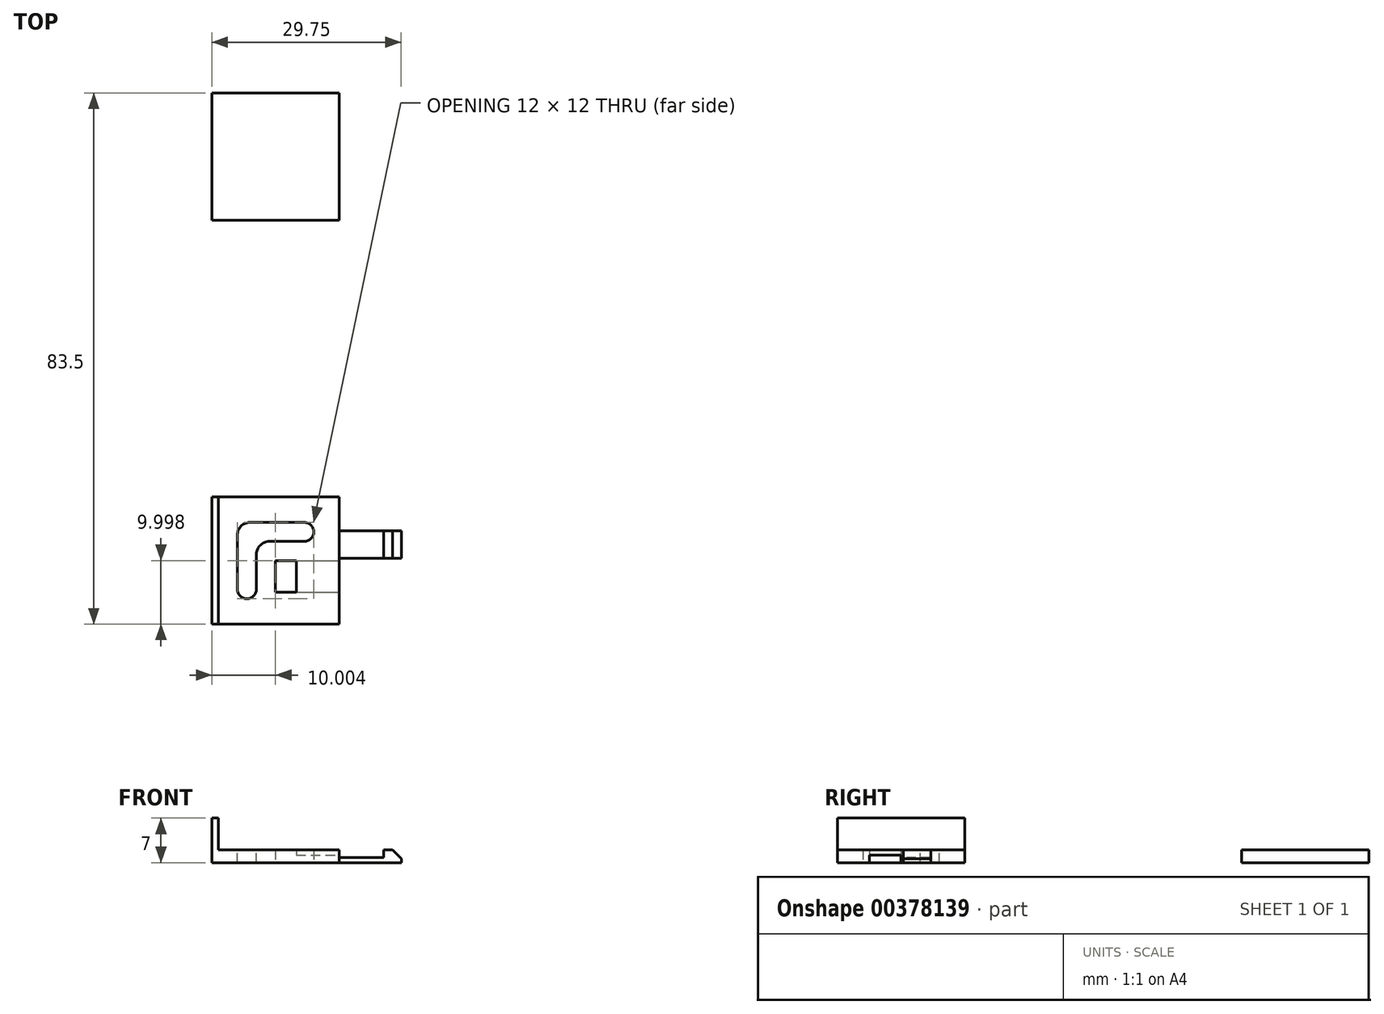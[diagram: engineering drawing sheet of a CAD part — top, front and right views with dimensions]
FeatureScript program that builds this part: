
annotation { "Feature Type Name" : "Feature", "Feature Type Description" : "" }
export const myFeature = defineFeature(function(context is Context, id is Id, definition is map)
    precondition{}
    {
        {
            var Q0;
            Q0=qCreatedBy(makeId("Top.planeOp"),FACE);
            var sketch = newSketch(context, id + "F0", { "sketchPlane" : qUnion([Q0])});
            skLineSegment(sketch, "E0.bottom", {"start": v(0.84, 22.12) * mm, "end": v(20.84, 22.12) * mm});
            skLineSegment(sketch, "E0.top", {"start": v(0.84, 42.12) * mm, "end": v(20.84, 42.12) * mm});
            skLineSegment(sketch, "E0.left", {"start": v(0.84, 22.12) * mm, "end": v(0.84, 42.12) * mm});
            skLineSegment(sketch, "E0.right", {"start": v(20.84, 22.12) * mm, "end": v(20.84, 42.12) * mm});
            skLineSegment(sketch, "E1.bottom", {"start": v(20.84, -21.38) * mm, "end": v(0.84, -21.38) * mm});
            skLineSegment(sketch, "E1.top", {"start": v(20.84, -41.38) * mm, "end": v(0.84, -41.38) * mm});
            skLineSegment(sketch, "E1.left", {"start": v(20.84, -21.38) * mm, "end": v(20.84, -41.38) * mm});
            skLineSegment(sketch, "E1.right", {"start": v(0.84, -21.38) * mm, "end": v(0.84, -41.38) * mm});
            skSolve(sketch);
        }
        {
            var Q0;
            Q0=makeQuery(id+"F0.imprint","IMPRINT",FACE,{"disambiguationData":[TD([[makeQuery(id+"F0.imprint","IMPRINT",EDGE,{"derivedFrom":sQuery(id+"F0.wireOp",EDGE,"E1.bottom")}),1.0]])]});
            var Q1;
            Q1=makeQuery(id+"F0.imprint","IMPRINT",FACE,{"disambiguationData":[TD([[makeQuery(id+"F0.imprint","IMPRINT",EDGE,{"derivedFrom":sQuery(id+"F0.wireOp",EDGE,"E0.bottom")}),1.0]])]});
            var Q2;
            Q2 = qSketchRegion(id + "F0", true);
            extrude(context, id + "F1", {"entities" : qUnion([Q0, Q1, Q2]), "depth" : 2 * mm});
        }
        {
            var Q0;
            Q0=makeQuery(id+"F1.opExtrude","SWEPT_FACE",FACE,{"disambiguationData":[OSD([sQuery(id+"F0.wireOp",EDGE,"E1.left")])]});
            var sketch = newSketch(context, id + "F2", { "sketchPlane" : qUnion([Q0])});
            skLineSegment(sketch, "E2.bottom", {"start": v(-36.38, 1.2) * mm, "end": v(-31.38, 1.2) * mm});
            skLineSegment(sketch, "E2.top", {"start": v(-36.38, 0) * mm, "end": v(-31.38, 0) * mm});
            skLineSegment(sketch, "E2.left", {"start": v(-36.38, 1.2) * mm, "end": v(-36.38, 0) * mm});
            skLineSegment(sketch, "E2.right", {"start": v(-31.38, 1.2) * mm, "end": v(-31.38, 0) * mm});
            skSolve(sketch);
        }
        {
            var Q0;
            Q0=makeQuery(id+"F2.imprint","IMPRINT",FACE,{"disambiguationData":[TD([[makeQuery(id+"F2.imprint","IMPRINT",EDGE,{"derivedFrom":sQuery(id+"F2.wireOp",EDGE,"E2.bottom")}),-1.0]])]});
            extrude(context, id + "F3", {"entities" : qUnion([Q0]), "operationType" : NewBodyOperationType.REMOVE, "oppositeDirection" : true, "depth" : 10 * mm});
        }
        {
            var Q0;
            Q0=makeQuery(id+"F3.boolean.opBoolean","COPY",FACE,{"derivedFrom":makeQuery(id+"F3.opExtrude","SWEPT_FACE",FACE,{"disambiguationData":[OSD([sQuery(id+"F2.wireOp",EDGE,"E2.bottom")])]})});
            var sketch = newSketch(context, id + "F4", { "sketchPlane" : qUnion([Q0])});
            skLineSegment(sketch, "E3.bottom", {"start": v(10.84, 36.38) * mm, "end": v(14.1, 36.38) * mm});
            skLineSegment(sketch, "E3.top", {"start": v(10.84, 31.38) * mm, "end": v(14.1, 31.38) * mm});
            skLineSegment(sketch, "E3.left", {"start": v(10.84, 36.38) * mm, "end": v(10.84, 31.38) * mm});
            skLineSegment(sketch, "E3.right", {"start": v(14.1, 36.38) * mm, "end": v(14.1, 31.38) * mm});
            skSolve(sketch);
        }
        {
            var Q0;
            Q0=makeQuery(id+"F4.imprint","IMPRINT",FACE,{"disambiguationData":[TD([[makeQuery(id+"F4.imprint","IMPRINT",EDGE,{"derivedFrom":sQuery(id+"F4.wireOp",EDGE,"E3.bottom")}),-1.0]])]});
            extrude(context, id + "F5", {"entities" : qUnion([Q0]), "operationType" : NewBodyOperationType.REMOVE, "endBound" : BoundingType.THROUGH_ALL, "oppositeDirection" : true, "depth" : 25 * mm});
        }
        {
            var Q0;
            Q0=makeQuery(id+"F1.opExtrude","SWEPT_FACE",FACE,{"disambiguationData":[OSD([sQuery(id+"F0.wireOp",EDGE,"E1.left")])]});
            var sketch = newSketch(context, id + "F6", { "sketchPlane" : qUnion([Q0])});
            skLineSegment(sketch, "E4.bottom", {"start": v(-26.73, 0.8) * mm, "end": v(-31.03, 0.8) * mm});
            skLineSegment(sketch, "E4.top", {"start": v(-26.73, 0) * mm, "end": v(-31.03, 0) * mm});
            skLineSegment(sketch, "E4.left", {"start": v(-26.73, 0.8) * mm, "end": v(-26.73, 0) * mm});
            skLineSegment(sketch, "E4.right", {"start": v(-31.03, 0.8) * mm, "end": v(-31.03, 0) * mm});
            skSolve(sketch);
        }
        {
            var Q0;
            Q0=makeQuery(id+"F6.imprint","IMPRINT",FACE,{"disambiguationData":[TD([[makeQuery(id+"F6.imprint","IMPRINT",EDGE,{"derivedFrom":sQuery(id+"F6.wireOp",EDGE,"E4.bottom")}),1.0]])]});
            extrude(context, id + "F7", {"entities" : qUnion([Q0]), "operationType" : NewBodyOperationType.ADD, "depth" : 9.75 * mm});
        }
        {
            var Q0;
            Q0=makeQuery(id+"F7.opExtrude","SWEPT_FACE",FACE,{"disambiguationData":[OSD([sQuery(id+"F6.wireOp",EDGE,"E4.bottom")])]});
            var sketch = newSketch(context, id + "F8", { "sketchPlane" : qUnion([Q0])});
            skLineSegment(sketch, "E5.bottom", {"start": v(30.6, -26.73) * mm, "end": v(27.84, -26.73) * mm});
            skLineSegment(sketch, "E5.top", {"start": v(30.6, -31.03) * mm, "end": v(27.84, -31.03) * mm});
            skLineSegment(sketch, "E5.left", {"start": v(30.6, -26.73) * mm, "end": v(30.6, -31.03) * mm});
            skLineSegment(sketch, "E5.right", {"start": v(27.84, -26.73) * mm, "end": v(27.84, -31.03) * mm});
            skSolve(sketch);
        }
        {
            var Q0;
            Q0=makeQuery(id+"F8.imprint","IMPRINT",FACE,{"disambiguationData":[TD([[makeQuery(id+"F8.imprint","IMPRINT",EDGE,{"derivedFrom":sQuery(id+"F8.wireOp",EDGE,"E5.bottom")}),1.0]])]});
            extrude(context, id + "F9", {"entities" : qUnion([Q0]), "operationType" : NewBodyOperationType.ADD, "depth" : 1.2 * mm});
        }
        {
            var Q0;
            Q0=makeQuery(id+"F9.opExtrude","CAP_EDGE",EDGE,{"disambiguationData":[OSD([sQuery(id+"F8.wireOp",EDGE,"E5.left")])],"isStart":false});
            chamfer(context, id + "F10", {"entities" : qUnion([Q0]), "width" : 1.4 * mm, "tangentPropagation" : true});
        }
        {
            var Q0;
            Q0=makeQuery(id+"F1.opExtrude","CAP_FACE",FACE,{"disambiguationData":[OSD([sQuery(id+"F0.wireOp",EDGE,"E1.bottom"),sQuery(id+"F0.wireOp",EDGE,"E1.top"),sQuery(id+"F0.wireOp",EDGE,"E1.left"),sQuery(id+"F0.wireOp",EDGE,"E1.right")])],"isStart":false});
            var sketch = newSketch(context, id + "F11", { "sketchPlane" : qUnion([Q0])});
            skLineSegment(sketch, "E6.bottom", {"start": v(0.84, -21.38) * mm, "end": v(1.84, -21.38) * mm});
            skLineSegment(sketch, "E6.top", {"start": v(0.84, -41.38) * mm, "end": v(1.84, -41.38) * mm});
            skLineSegment(sketch, "E6.left", {"start": v(0.84, -21.38) * mm, "end": v(0.84, -41.38) * mm});
            skLineSegment(sketch, "E6.right", {"start": v(1.84, -21.38) * mm, "end": v(1.84, -41.38) * mm});
            skSolve(sketch);
        }
        {
            var Q0;
            Q0 = qSketchRegion(id + "F11", true);
            var Q1;
            Q1=makeQuery(id+"F11.imprint","IMPRINT",FACE,{"disambiguationData":[TD([[makeQuery(id+"F11.imprint","IMPRINT",EDGE,{"derivedFrom":sQuery(id+"F11.wireOp",EDGE,"E6.bottom")}),1.0]])]});
            extrude(context, id + "F12", {"entities" : qUnion([Q0, Q1]), "operationType" : NewBodyOperationType.ADD, "depth" : 5 * mm});
        }
        {
            var Q0;
            Q0=makeQuery(id+"F1.opExtrude","CAP_FACE",FACE,{"disambiguationData":[OSD([sQuery(id+"F0.wireOp",EDGE,"E1.bottom"),sQuery(id+"F0.wireOp",EDGE,"E1.top"),sQuery(id+"F0.wireOp",EDGE,"E1.left"),sQuery(id+"F0.wireOp",EDGE,"E1.right")])],"isStart":false});
            var sketch = newSketch(context, id + "F13", { "sketchPlane" : qUnion([Q0])});
            skLineSegment(sketch, "E7", {"start": v(4.84, -37.38) * mm, "end": v(4.84, -25.38) * mm});
            skLineSegment(sketch, "E8", {"start": v(4.84, -25.38) * mm, "end": v(16.84, -25.38) * mm});
            skLineSegment(sketch, "E9", {"start": v(16.84, -25.38) * mm, "end": v(16.84, -28.38) * mm});
            skLineSegment(sketch, "E10", {"start": v(16.84, -28.38) * mm, "end": v(7.84, -28.38) * mm});
            skLineSegment(sketch, "E11", {"start": v(7.84, -28.38) * mm, "end": v(7.84, -37.38) * mm});
            skLineSegment(sketch, "E12", {"start": v(7.84, -37.38) * mm, "end": v(4.84, -37.38) * mm});
            skSolve(sketch);
        }
        {
            var Q0;
            Q0=makeQuery(id+"F13.imprint","IMPRINT",FACE,{"disambiguationData":[TD([[makeQuery(id+"F13.imprint","IMPRINT",EDGE,{"derivedFrom":sQuery(id+"F13.wireOp",EDGE,"E7")}),-1.0]])]});
            extrude(context, id + "F14", {"entities" : qUnion([Q0]), "operationType" : NewBodyOperationType.REMOVE, "endBound" : BoundingType.THROUGH_ALL, "oppositeDirection" : true, "depth" : 25 * mm});
        }
        {
            var Q0;
            Q0=makeQuery(id+"F14.boolean.opBoolean","COPY",EDGE,{"derivedFrom":makeQuery(id+"F14.opExtrude","SWEPT_EDGE",EDGE,{"disambiguationData":[OSD([sQuery(id+"F13.wireOp",EDGE,"E10"),sQuery(id+"F13.wireOp",EDGE,"E11")])]})});
            var Q1;
            Q1=makeQuery(id+"F14.boolean.opBoolean","COPY",EDGE,{"derivedFrom":makeQuery(id+"F14.opExtrude","SWEPT_EDGE",EDGE,{"disambiguationData":[OSD([sQuery(id+"F13.wireOp",EDGE,"E7"),sQuery(id+"F13.wireOp",EDGE,"E8")])]})});
            fillet(context, id + "F15", {"entities" : qUnion([Q0, Q1]), "radius" : 2 * mm, "tangentPropagation" : true, "allowEdgeOverflow" : false});
        }
        {
            var Q0;
            Q0=makeQuery(id+"F14.boolean.opBoolean","COPY",EDGE,{"derivedFrom":makeQuery(id+"F14.opExtrude","SWEPT_EDGE",EDGE,{"disambiguationData":[OSD([sQuery(id+"F13.wireOp",EDGE,"E7"),sQuery(id+"F13.wireOp",EDGE,"E12")])]})});
            var Q1;
            Q1=makeQuery(id+"F14.boolean.opBoolean","COPY",EDGE,{"derivedFrom":makeQuery(id+"F14.opExtrude","SWEPT_EDGE",EDGE,{"disambiguationData":[OSD([sQuery(id+"F13.wireOp",EDGE,"E11"),sQuery(id+"F13.wireOp",EDGE,"E12")])]})});
            var Q2;
            Q2=makeQuery(id+"F14.boolean.opBoolean","COPY",EDGE,{"derivedFrom":makeQuery(id+"F14.opExtrude","SWEPT_EDGE",EDGE,{"disambiguationData":[OSD([sQuery(id+"F13.wireOp",EDGE,"E9"),sQuery(id+"F13.wireOp",EDGE,"E10")])]})});
            var Q3;
            Q3=makeQuery(id+"F14.boolean.opBoolean","COPY",EDGE,{"derivedFrom":makeQuery(id+"F14.opExtrude","SWEPT_EDGE",EDGE,{"disambiguationData":[OSD([sQuery(id+"F13.wireOp",EDGE,"E8"),sQuery(id+"F13.wireOp",EDGE,"E9")])]})});
            fillet(context, id + "F16", {"entities" : qUnion([Q0, Q1, Q2, Q3]), "radius" : 1.5 * mm, "tangentPropagation" : true, "allowEdgeOverflow" : false});
        }
    });
